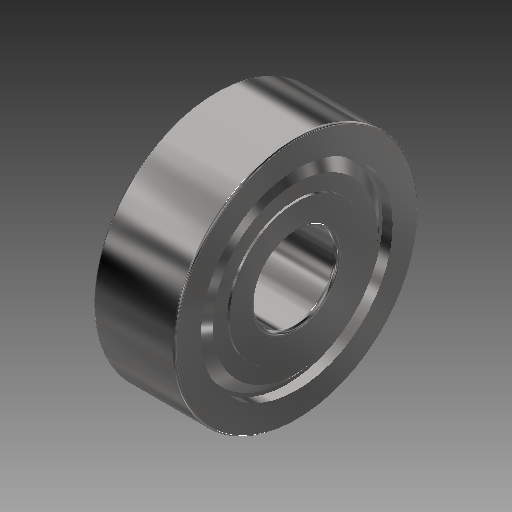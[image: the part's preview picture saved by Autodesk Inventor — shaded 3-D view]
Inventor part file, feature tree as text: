
AUTODESK INVENTOR PART (.ipt)
format: ipt  version: 2018 (Build 220112000, 112)  size: 706,560 bytes
history: native  units: in
note: dims shown in document units (in); Inventor stores cm internally (conversion verified against a paired STEP export)
features: other x11, imported_body x10, extrude x1, fillet x1, sketch x1
ambient origin geometry x8: Origin, YZ Plane, XZ Plane, XY Plane, X Axis, Y Axis, Z Axis, Center Point
bodies: Body1 (feature_tree), Body2 (feature_tree), Body3 (feature_tree), Body4 (feature_tree), Body5 (feature_tree), Body6 (feature_tree), Body7 (feature_tree), Body8 (feature_tree), Body9 (feature_tree), Body10 (feature_tree)
feature tree (24):
  other  "1614ZZ"
  other  "1614ZZ1"
  extrude  "Extrusion1"  Depth=0.01in
  fillet  "Fillet1"  [1 undecoded]
  other  "1614ZZ_1"
  other  "1614ZZ_2"
  other  "1614ZZ_3"
  other  "1614ZZ_4"
  other  "1614ZZ_5"
  other  "1614ZZ_6"
  other  "1614ZZ_7"
  other  "1614ZZ_8"
  other  "1614ZZ_9"
  imported_body  "Base1"
  imported_body  "Base2"
  imported_body  "Base3"
  imported_body  "Base4"
  imported_body  "Base5"
  imported_body  "Base6"
  imported_body  "Base7"
  imported_body  "Base8"
  imported_body  "Base9"
  imported_body  "Base10"
  sketch  "Sketch1"  dims[d0=1.0in d1=0.0in d2=0.01in]
note: 1 required parameter value undecoded (feature->parameter linkage not recoverable at this tier; creation-order binding heuristic only, values carry confidence <= 0.55)
